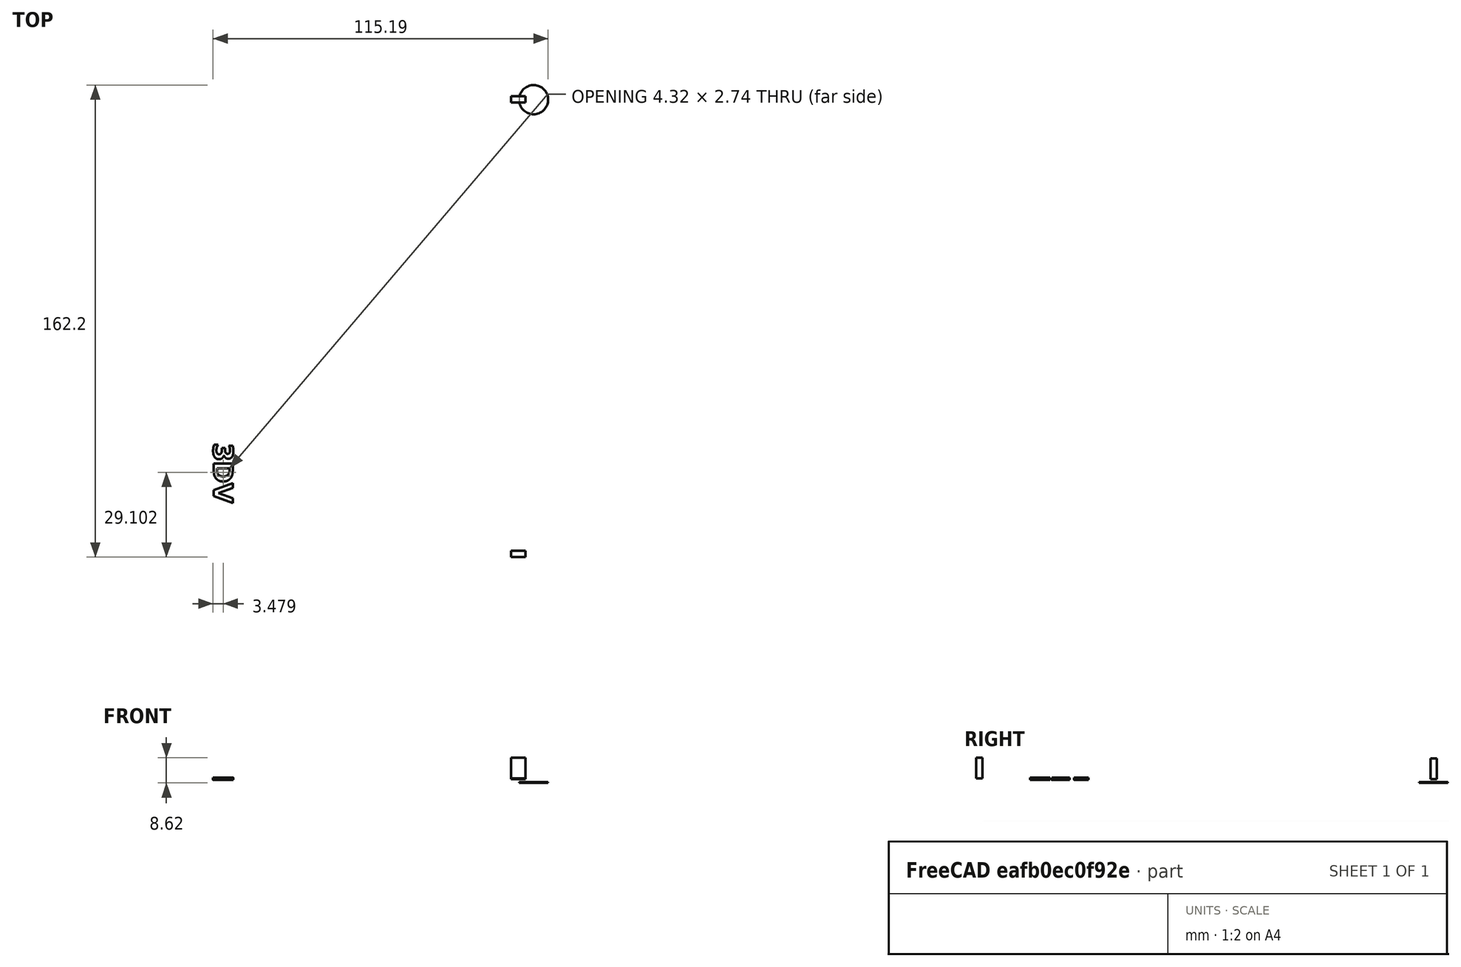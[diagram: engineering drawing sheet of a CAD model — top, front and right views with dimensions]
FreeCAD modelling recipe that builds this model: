
FCSTD DOCUMENT  (FreeCAD 0.18.3R)
Label: visera_original_con_adhesión
License: All rights reserved
LicenseURL: http://en.wikipedia.org/wiki/All_rights_reserved
objects: Sketcher::SketchObject×2, PartDesign::Pad×2, PartDesign::Body×2, Part::Mirroring×2, Mesh::Feature×1, Part::Part2DObjectPython×1, Part::Extrusion×1
note: 12 computed .brp shape members not serialized (recipe doc carries the construction recipe); baked Part::Feature solids carry a one-line shape summary decoded from their .brp

FEATURE [Mesh::Feature] Visera_Plana_con_cierre_y_ventilacion_0_6  label="Visera_Plana_con_cierre_y_ventilacion_0.6"
  Placement = pos=(-168,-22,0) rot=(0,0,1;0rad)
FEATURE [Sketcher::SketchObject] Sketch
  MapMode = 5
  Support = -> [XY_Plane]
  sketch-geometry (1):
    g0: Circle CenterX=0 CenterY=0 CenterZ=0 NormalX=0 NormalY=0 NormalZ=1 AngleXU=0 Radius=5
  constraints (2):
    c: Coincident(g0,g-1)
    c: Radius(g0) = 5
FEATURE [PartDesign::Pad] Pad
  Length = 0.3
  Length2 = 100
  Profile = -> Sketch
  Refine = true
  Type = 0
FEATURE [PartDesign::Body] Body
  Group = -> [Sketch,Pad]
  Origin = -> Origin
  Tip = -> Pad
FEATURE [Part::Mirroring] Part__Mirroring  label="Body (Mirror #1)"
  Base = (0,10,0)
  Normal = (0,1,0)
  Placement = pos=(0,136,0) rot=(0,0,1;0rad)
  Source = -> Body
FEATURE [Part::Part2DObjectPython] ShapeString  # Draft 2D object (typed FeaturePython)
  FontFile = <path>
  Placement = pos=(0,0,1) rot=(0.661067,-0.632283,0.403991;0rad)
  Size = 7
  String = 3DV
  Tracking = 0
FEATURE [Part::Extrusion] Extrude
  Base = -> ShapeString
  Dir = (0,0,1)
  DirMode = 2
  FaceMakerClass = Part::FaceMakerBullseye
  LengthFwd = 0.8
  LengthRev = 0
  Placement = pos=(-110,38,0) rot=(0,0,-1;1.5708rad)
  Solid = false
  Symmetric = false
FEATURE [Sketcher::SketchObject] Sketch001
  MapMode = 5
  Placement = pos=(0,0,0) rot=(1,0,0;1.5708rad)
  Support = -> [XZ_Plane001]
  sketch-geometry (4):
    g0: LineSegment StartX=-7.8 StartY=8.62 StartZ=0 EndX=-2.8 EndY=8.62 EndZ=0
    g1: LineSegment StartX=-2.8 StartY=8.62 StartZ=0 EndX=-2.8 EndY=1.62 EndZ=0
    g2: LineSegment StartX=-2.8 StartY=1.62 StartZ=0 EndX=-7.8 EndY=1.62 EndZ=0
    g3: LineSegment StartX=-7.8 StartY=1.62 StartZ=0 EndX=-7.8 EndY=8.62 EndZ=0
  constraints (12):
    c: Coincident(g0,g1)
    c: Coincident(g1,g2)
    c: Coincident(g2,g3)
    c: Coincident(g3,g0)
    c: Horizontal(g0)
    c: Horizontal(g2)
    c: Vertical(g1)
    c: Vertical(g3)
    c: DistanceY(g3,g3) = 7
    c: DistanceX(g0,g0) = 5
    c: DistanceX(g1,g-1) = 2.8
    c: DistanceY(g-1,g1) = 1.62
FEATURE [PartDesign::Pad] Pad001
  Length = 2.2
  Length2 = 100
  Midplane = true
  Placement = pos=(0,0,0) rot=(1,0,0;1.5708rad)
  Profile = -> Sketch001
  Refine = true
  Type = 0
FEATURE [PartDesign::Body] Body001  label="Tapones"
  Group = -> [Sketch001,Pad001]
  Origin = -> Origin001
  Placement = pos=(0,-0.1,0) rot=(0,0,1;0rad)
  Tip = -> Pad001
FEATURE [Part::Mirroring] Part__Mirroring001  label="Pad001 (Mirror #2)"
  Base = (-5.3,3.4e-15,0)
  Normal = (0,0,1)
  Placement = pos=(0,156.1,10) rot=(0,0,1;0rad)
  Source = -> Pad001
note: 1 file-system path scrubbed to <path> (originals preserved in the JSON sidecar)
